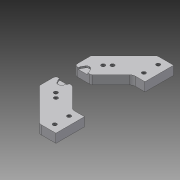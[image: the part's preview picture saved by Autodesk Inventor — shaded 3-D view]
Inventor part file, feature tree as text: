
AUTODESK INVENTOR PART (.ipt)
format: ipt  version: 2014 (Build 180170000, 170)  size: 249,344 bytes
history: native  units: in
note: dims shown in document units (in); Inventor stores cm internally (conversion verified against a paired STEP export)
features: fillet x9, sketch x5, projected_geometry x4, plane x2, extrude x2, chamfer x2, hole x2, mirror x1, other x1
ambient origin geometry x8: Origin, YZ Plane, XZ Plane, XY Plane, X Axis, Y Axis, Z Axis, Center Point
bodies: Solid1 (feature_tree), Solid2 (feature_tree)
feature tree (28):
  plane  "Work Plane1"
  extrude  "Extrusion1"  Depth=0.65in
  extrude  "Extrusion2"  Depth=0.375in
  chamfer  "Chamfer1"  Distance=0.09in
  chamfer  "Chamfer2"  Distance=0.04in
  sketch  "Sketch4"  dims[d7=0.0in]
  sketch  "Sketch5"  dims[d8=0.209in]
  hole  "Connection"  [1 undecoded]
  sketch  "Sketch6"  dims[d9=0.14in d10=0.09in d11=0.04in d12=0.0in d13=0.0626in d14=0.125in d15=60.0deg d16=0.0626in d17=0.125in d18=60.0deg d27=0.7874in d29=0.1625in d30=0.7874in d32=0.1625in d35=0.0849in d36=0.75in d37=0.375in d38=0.25in d39=0.5635in d40=1.0in d41=0.8108in d42=0.4in d51=0.195in d74=0.3in d75=0.15in d76=0.0849in d77=0.75in d78=0.375in d79=0.25in d80=0.5635in d81=1.0in d82=0.8108in d83=0.0625in d84=0.0625in d85=0.0625in d86=0.0625in d87=0.125in d88=0.125in d89=0.0625in d90=0.0625in d91=0.0625in d50=1.0in]
  hole  "Hole7"  [1 undecoded]
  fillet  "Fillet1"  Radius=0.7874in
  fillet  "Fillet2"  Radius=0.7874in
  fillet  "Fillet3"  Radius=0.4in
  fillet  "Fillet4"  Radius=0.195in
  fillet  "Fillet5"  Radius=0.3in
  fillet  "Fillet6"  Radius=0.15in
  fillet  "Fillet7"  Radius=0.0625in
  fillet  "Fillet8"  Radius=0.0625in
  fillet  "Fillet9"  Radius=0.0625in
  mirror  "Mirror2"
  sketch  "Sketch2"  dims[d1=0.375in d3=0.65in]
  sketch  "Sketch3"  dims[d4=0.75in d5=0.375in]
  projected_geometry  "Projected Loop1"
  projected_geometry  "Projected Loop3"
  other  "Pattern of Solid1:1"
  plane  "Work Plane2"
  projected_geometry  "Projected Loop4"
  projected_geometry  "Projected Loop5"
note: 2 required parameter values undecoded (feature->parameter linkage not recoverable at this tier; creation-order binding heuristic only, values carry confidence <= 0.55)
